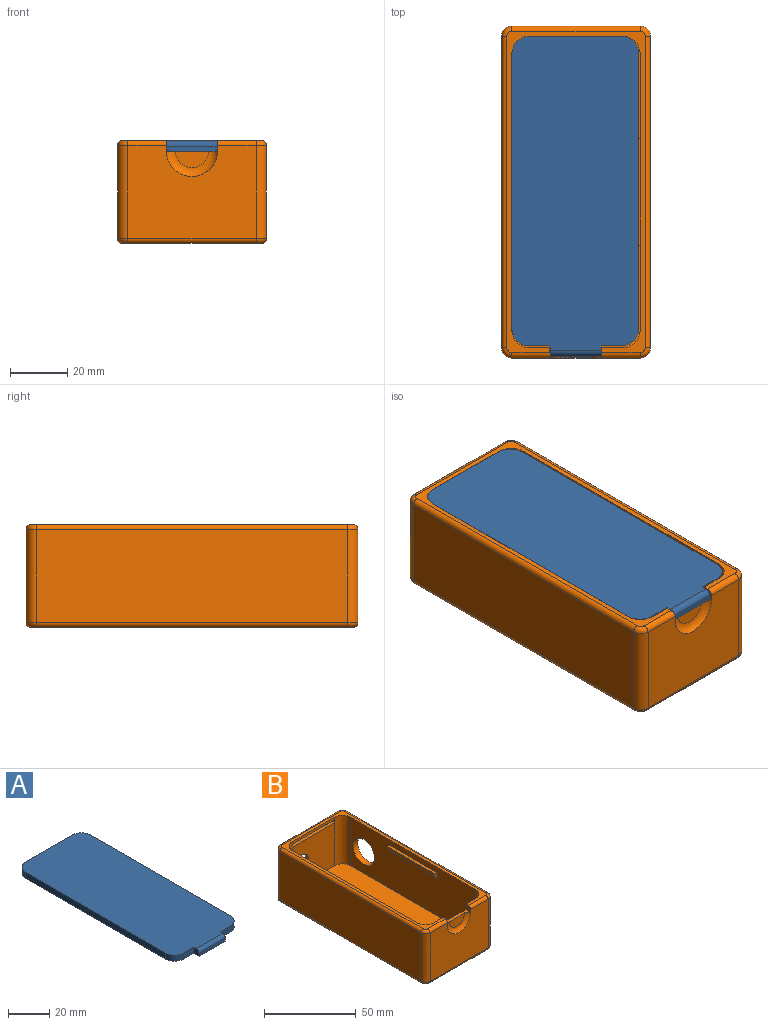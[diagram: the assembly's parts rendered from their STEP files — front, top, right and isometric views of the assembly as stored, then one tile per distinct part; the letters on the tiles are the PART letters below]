
ASSEMBLY  parts=2 mates=1
PART A: 20 faces, bbox 44.3x113.7x3.6 mm
  f0: plane 7.15x3.6mm, normal (0,-1,0), area 25.7mm2, adj f5,f9,f10,f12
  f1: cylinder r=6mm len=6mm, axis (0,0,-1), area 33.9mm2, adj f2,f8,f9,f10,f15
  f2: plane 32.3x1.8mm, normal (0,1,0), area 58.1mm2, adj f1,f3,f9,f14
  f3: cylinder r=6mm len=6mm, axis (0,0,-1), area 33.9mm2, adj f2,f4,f9,f10,f16
  f4: plane 96.31x3.6mm, normal (-1,0,0), area 346.7mm2, adj f3,f5,f9,f10
  f5: cylinder r=6mm len=6mm, axis (0,0,-1), area 33.9mm2, adj f0,f4,f9,f10
  f6: plane 7.15x3.6mm, normal (0,-1,0), area 25.7mm2, adj f7,f9,f10,f11
  f7: cylinder r=6mm len=6mm, axis (0,0,-1), area 33.9mm2, adj f6,f8,f9,f10
  f8: plane 96.31x3.6mm, normal (1,0,0), area 346.7mm2, adj f1,f7,f9,f10
  f9: plane 110x44.3mm, normal (0,0,1), area 4797.4mm2, adj f0,f1,f2,f3,f4,f5,f6,f7
  f10: plane 113.7x44.3mm, normal (0,0,-1), area 4889.8mm2, adj f0,f1,f3,f4,f5,f6,f7,f8
  f11: plane 3.6x3.6mm, normal (1,0,0), area 12.2mm2, adj f6,f9,f10,f13,f18
  f12: plane 3.6x3.6mm, normal (-1,0,0), area 12.2mm2, adj f0,f9,f10,f13,f18
  f13: plane 18x1.7mm, normal (0,-1,0), area 30.6mm2, adj f10,f11,f12,f18
  f14: plane 32.3x1.3mm, normal (0,0,1), area 42mm2, adj f2,f15,f16,f19
  f15: plane 1.8x1.8mm, normal (1,0,0), area 3.2mm2, adj f1,f10,f14,f17,f19
  f16: plane 1.8x1.8mm, normal (-1,0,0), area 3.2mm2, adj f3,f10,f14,f17,f19
  f17: plane 32.3x1.3mm, normal (0,1,0), area 42mm2, adj f10,f15,f16,f19
  f18: cylinder r=1.9mm len=18mm, axis (-1,0,0), area 53.7mm2, adj f9,f11,f12,f13
  f19: cylinder r=0.5mm len=32.3mm, axis (-1,0,0), area 25.4mm2, adj f14,f15,f16,f17
PART B: 62 faces, bbox 52.6x118.1x36 mm
  f0: plane 96.81x32.4mm, normal (1,0,0), area 2998.7mm2, adj f4,f11,f16,f17,f52,f57,f58,f59
  f1: plane 96.81x32.4mm, normal (-1,0,0), area 2784.8mm2, adj f4,f11,f18,f19,f21,f50,f54,f55
  f2: plane 44.8x32.4mm, normal (0,1,0), area 999.1mm2, adj f12,f13,f34,f44,f47
  f3: plane 32.8x1.7mm, normal (0,-1,0), area 55.8mm2, adj f4,f17,f18,f28
  f4: plane 112.4x48.4mm, normal (0,0,1), area 561.6mm2, adj f0,f1,f3,f5,f16,f17,f18,f19
  f5: plane 32.8x32.4mm, normal (0,1,0), area 998.1mm2, adj f4,f11,f16,f19,f22,f23,f24
  f6: plane 44.8x32.4mm, normal (0,-1,0), area 1291.9mm2, adj f14,f15,f22,f24,f30,f38,f41,f61
  f7: plane 32.8x28.7mm, normal (0,-1,0), area 854.9mm2, adj f11,f17,f18,f20,f26
  f8: plane 108.8x32.4mm, normal (1,0,0), area 3311.3mm2, adj f12,f15,f21,f32,f45
  f9: plane 108.8x32.4mm, normal (-1,0,0), area 3525.1mm2, adj f13,f14,f36,f40
  f10: plane 112.4x48.4mm, normal (0,0,-1), area 5437.4mm2, adj f39,f40,f41,f42,f43,f44,f45,f46
  f11: plane 108.8x44.8mm, normal (0,0,1), area 4843.4mm2, adj f0,f1,f5,f7,f16,f17,f18,f19
  f12: cylinder r=3.6mm len=32.4mm, axis (0,0,-1), area 183.2mm2, adj f2,f8,f33,f46
  f13: cylinder r=3.6mm len=32.4mm, axis (0,0,1), area 183.2mm2, adj f2,f9,f35,f42
  f14: cylinder r=3.6mm len=32.4mm, axis (0,0,-1), area 183.2mm2, adj f6,f9,f37,f39
  f15: cylinder r=3.6mm len=32.4mm, axis (0,0,1), area 183.2mm2, adj f6,f8,f31,f43
  f16: cylinder r=6mm len=32.4mm, axis (0,0,1), area 305.2mm2, adj f0,f4,f5,f11
  f17: cylinder r=6mm len=32.4mm, axis (0,0,-1), area 305.2mm2, adj f0,f3,f4,f7,f11,f25
  f18: cylinder r=6mm len=32.4mm, axis (0,0,1), area 305.2mm2, adj f1,f3,f4,f7,f11,f27
  f19: cylinder r=6mm len=32.4mm, axis (0,0,-1), area 305.2mm2, adj f1,f4,f5,f11
  f20: cylinder r=5.25mm len=10.5mm, axis (0,1,0), area 85.8mm2, adj f7,f48
  f21: cylinder r=8.25mm len=16.5mm, axis (1,0,0), area 186.6mm2, adj f1,f8
  f22: plane 3.6x3.6mm, normal (1,0,0), area 12.3mm2, adj f4,f5,f6,f23,f38
  f23: plane 18x3.6mm, normal (0,0,1), area 35.7mm2, adj f5,f22,f24,f60,f61
  f24: plane 3.6x3.6mm, normal (-1,0,0), area 12.3mm2, adj f4,f5,f6,f23,f30
  f25: plane 2.1x2mm, normal (1,0,0), area 4.1mm2, adj f17,f26,f28,f29,f49
  f26: plane 32.8x2.1mm, normal (0,0,1), area 68.9mm2, adj f7,f25,f27,f29
  f27: plane 2.1x2mm, normal (-1,0,0), area 4.1mm2, adj f18,f26,f28,f29,f49
  f28: plane 32.8x1.6mm, normal (0,0,-1), area 52.5mm2, adj f3,f25,f27,f49
  f29: plane 32.8x1.5mm, normal (0,-1,0), area 49.2mm2, adj f25,f26,f27,f49
  f30: cylinder r=1.8mm len=13.4mm, axis (-1,0,0), area 37.9mm2, adj f4,f6,f24,f31
  f31: torus R=1.8mm, axis (0,0,1), area 13.1mm2, adj f4,f15,f30,f32
  f32: cylinder r=1.8mm len=108.8mm, axis (0,-1,0), area 307.6mm2, adj f4,f8,f31,f33
  f33: torus R=1.8mm, axis (0,0,1), area 13.1mm2, adj f4,f12,f32,f34
  f34: cylinder r=1.8mm len=44.8mm, axis (1,0,0), area 126.7mm2, adj f2,f4,f33,f35
  f35: torus R=1.8mm, axis (0,0,1), area 13.1mm2, adj f4,f13,f34,f36
  f36: cylinder r=1.8mm len=108.8mm, axis (0,1,0), area 307.6mm2, adj f4,f9,f35,f37
  f37: torus R=1.8mm, axis (0,0,1), area 13.1mm2, adj f4,f14,f36,f38
  f38: cylinder r=1.8mm len=13.4mm, axis (-1,0,0), area 37.9mm2, adj f4,f6,f22,f37
  f39: torus R=1.8mm, axis (0,0,1), area 13.1mm2, adj f10,f14,f40,f41
  f40: cylinder r=1.8mm len=108.8mm, axis (0,-1,0), area 307.6mm2, adj f9,f10,f39,f42
  f41: cylinder r=1.8mm len=44.8mm, axis (1,0,0), area 126.7mm2, adj f6,f10,f39,f43
  f42: torus R=1.8mm, axis (0,0,1), area 13.1mm2, adj f10,f13,f40,f44
  f43: torus R=1.8mm, axis (0,0,1), area 13.1mm2, adj f10,f15,f41,f45
  f44: cylinder r=1.8mm len=44.8mm, axis (-1,0,0), area 126.7mm2, adj f2,f10,f42,f46
  f45: cylinder r=1.8mm len=108.8mm, axis (0,1,0), area 307.6mm2, adj f8,f10,f43,f46
  f46: torus R=1.8mm, axis (0,0,1), area 13.1mm2, adj f10,f12,f44,f45
  f47: cylinder r=12mm len=24mm, axis (0,1,0), area 75.4mm2, adj f2,f48
  f48: plane 24x24mm, normal (0,1,0), area 365.8mm2, adj f20,f47
  f49: cylinder r=0.5mm len=32.8mm, axis (-1,0,0), area 25.8mm2, adj f25,f27,f28,f29
  f50: plane 38.28x1.8mm, normal (0,0,1), area 65.7mm2, adj f1,f51,f54,f56
  f51: plane 34.68x1.8mm, normal (-1,0,0), area 62.4mm2, adj f50,f54,f55,f56
  f52: plane 38.28x1.8mm, normal (0,0,1), area 65.7mm2, adj f0,f53,f57,f59
  f53: plane 34.68x1.8mm, normal (1,0,0), area 62.4mm2, adj f52,f57,f58,f59
  f54: plane 3.6x1.8mm, normal (-0.71,0.71,0), area 6.9mm2, adj f1,f50,f51,f55
  f55: plane 38.28x1.8mm, normal (-0.71,0,-0.71), area 92.9mm2, adj f1,f51,f54,f56
  f56: plane 3.6x1.8mm, normal (-0.71,-0.71,0), area 6.9mm2, adj f1,f50,f51,f55
  f57: plane 3.6x1.8mm, normal (0.71,-0.71,0), area 6.9mm2, adj f0,f52,f53,f58
  f58: plane 38.28x1.8mm, normal (0.71,0,-0.71), area 92.9mm2, adj f0,f53,f57,f59
  f59: plane 3.6x1.8mm, normal (0.71,0.71,0), area 6.9mm2, adj f0,f52,f53,f58
  f60: plane 11.76x5.88mm, normal (0,-1,0), area 54.4mm2, adj f23,f61
  f61: torus R=5.88mm, axis (0,1,0), area 90mm2, adj f6,f23,f60
PLACE A t=(34.26,21.24,1.45)mm
PLACE B t=(34.51,20.94,-30.85)mm
MATE fastened B.f26 <-> A.f10  axis (0,0,1) through (18.11,77.44,1.45)mm
